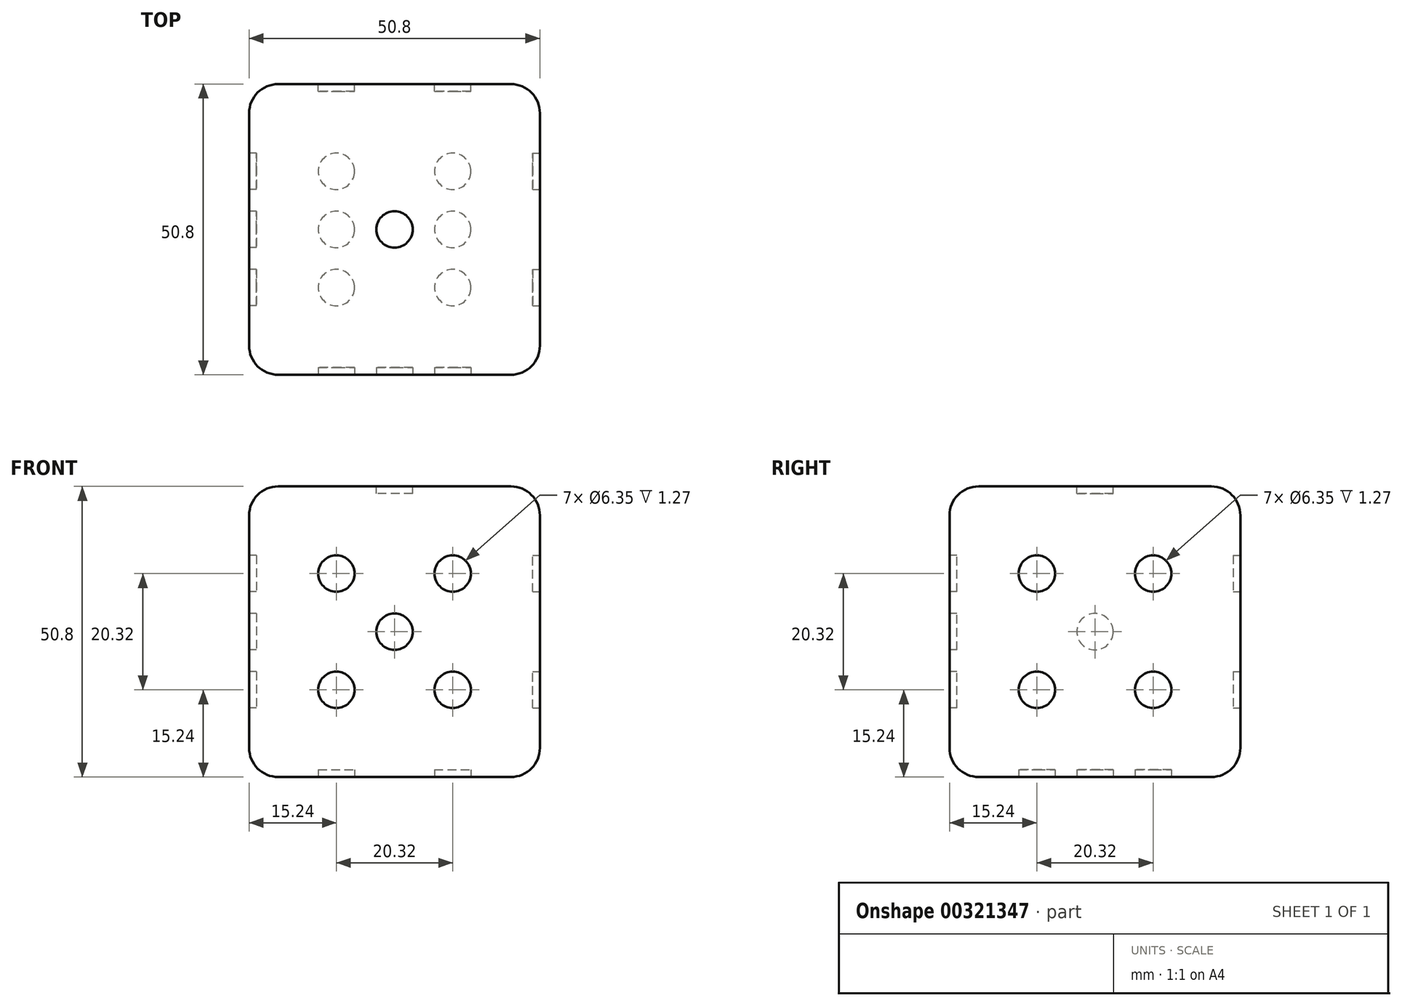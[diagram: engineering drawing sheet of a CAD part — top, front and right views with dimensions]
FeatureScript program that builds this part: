
annotation { "Feature Type Name" : "Feature", "Feature Type Description" : "" }
export const myFeature = defineFeature(function(context is Context, id is Id, definition is map)
    precondition{}
    {
        {
            var Q0;
            Q0=qCreatedBy(makeId("Top.planeOp"),FACE);
            var sketch = newSketch(context, id + "F0", { "sketchPlane" : qUnion([Q0])});
            skLineSegment(sketch, "E0.bottom", {"start": v(0, 0) * mm, "end": v(50.8, 0) * mm});
            skLineSegment(sketch, "E0.top", {"start": v(0, -50.8) * mm, "end": v(50.8, -50.8) * mm});
            skLineSegment(sketch, "E0.left", {"start": v(0, 0) * mm, "end": v(0, -50.8) * mm});
            skLineSegment(sketch, "E0.right", {"start": v(50.8, 0) * mm, "end": v(50.8, -50.8) * mm});
            skSolve(sketch);
        }
        {
            var Q0;
            Q0=makeQuery(id+"F0.imprint","IMPRINT",FACE,{"disambiguationData":[TD([[makeQuery(id+"F0.imprint","IMPRINT",EDGE,{"derivedFrom":sQuery(id+"F0.wireOp",EDGE,"E0.bottom")}),-1.0]])]});
            extrude(context, id + "F1", {"entities" : qUnion([Q0]), "depth" : 50.8 * mm});
        }
        {
            var Q0;
            Q0=makeQuery(id+"F1.opExtrude","SWEPT_EDGE",EDGE,{"disambiguationData":[OSD([sQuery(id+"F0.wireOp",EDGE,"E0.top"),sQuery(id+"F0.wireOp",EDGE,"E0.right")])]});
            var Q1;
            Q1=makeQuery(id+"F1.opExtrude","CAP_EDGE",EDGE,{"disambiguationData":[OSD([sQuery(id+"F0.wireOp",EDGE,"E0.right")])],"isStart":false});
            var Q2;
            Q2=makeQuery(id+"F1.opExtrude","CAP_EDGE",EDGE,{"disambiguationData":[OSD([sQuery(id+"F0.wireOp",EDGE,"E0.right")])],"isStart":true});
            var Q3;
            Q3=makeQuery(id+"F1.opExtrude","CAP_EDGE",EDGE,{"disambiguationData":[OSD([sQuery(id+"F0.wireOp",EDGE,"E0.top")])],"isStart":true});
            var Q4;
            Q4=makeQuery(id+"F1.opExtrude","CAP_EDGE",EDGE,{"disambiguationData":[OSD([sQuery(id+"F0.wireOp",EDGE,"E0.top")])],"isStart":false});
            var Q5;
            Q5=makeQuery(id+"F1.opExtrude","SWEPT_EDGE",EDGE,{"disambiguationData":[OSD([sQuery(id+"F0.wireOp",EDGE,"E0.top"),sQuery(id+"F0.wireOp",EDGE,"E0.left")])]});
            var Q6;
            Q6=makeQuery(id+"F1.opExtrude","SWEPT_EDGE",EDGE,{"disambiguationData":[OSD([sQuery(id+"F0.wireOp",EDGE,"E0.bottom"),sQuery(id+"F0.wireOp",EDGE,"E0.right")])]});
            var Q7;
            Q7=makeQuery(id+"F1.opExtrude","SWEPT_EDGE",EDGE,{"disambiguationData":[OSD([sQuery(id+"F0.wireOp",EDGE,"E0.bottom"),sQuery(id+"F0.wireOp",EDGE,"E0.left")])]});
            var Q8;
            Q8=makeQuery(id+"F1.opExtrude","CAP_EDGE",EDGE,{"disambiguationData":[OSD([sQuery(id+"F0.wireOp",EDGE,"E0.bottom")])],"isStart":false});
            var Q9;
            Q9=makeQuery(id+"F1.opExtrude","CAP_EDGE",EDGE,{"disambiguationData":[OSD([sQuery(id+"F0.wireOp",EDGE,"E0.bottom")])],"isStart":true});
            var Q10;
            Q10=makeQuery(id+"F1.opExtrude","CAP_EDGE",EDGE,{"disambiguationData":[OSD([sQuery(id+"F0.wireOp",EDGE,"E0.left")])],"isStart":false});
            var Q11;
            Q11=makeQuery(id+"F1.opExtrude","CAP_EDGE",EDGE,{"disambiguationData":[OSD([sQuery(id+"F0.wireOp",EDGE,"E0.left")])],"isStart":true});
            var Q12;
            Q12=makeQuery(id+"F1.opExtrude","CAP_FACE",FACE,{"disambiguationData":[OSD([sQuery(id+"F0.wireOp",EDGE,"E0.bottom"),sQuery(id+"F0.wireOp",EDGE,"E0.top"),sQuery(id+"F0.wireOp",EDGE,"E0.left"),sQuery(id+"F0.wireOp",EDGE,"E0.right")])],"isStart":false});
            fillet(context, id + "F2", {"entities" : qUnion([Q0, Q1, Q2, Q3, Q4, Q5, Q6, Q7, Q8, Q9, Q10, Q11, Q12]), "radius" : 5.08 * mm, "tangentPropagation" : true, "allowEdgeOverflow" : false});
        }
        {
            var Q0;
            Q0=makeQuery(id+"F1.opExtrude","CAP_FACE",FACE,{"disambiguationData":[OSD([sQuery(id+"F0.wireOp",EDGE,"E0.bottom"),sQuery(id+"F0.wireOp",EDGE,"E0.top"),sQuery(id+"F0.wireOp",EDGE,"E0.left"),sQuery(id+"F0.wireOp",EDGE,"E0.right")])],"isStart":false});
            var sketch = newSketch(context, id + "F3", { "sketchPlane" : qUnion([Q0])});
            skLineSegment(sketch, "E1", {"start": v(25.4, -5.08) * mm, "end": v(25.4, -45.72) * mm, "construction": true});
            skCircle(sketch, "E2", {"center": v(25.4, -25.4) * mm, "radius": 3.18 * mm});
            skSolve(sketch);
        }
        {
            var Q0;
            Q0=makeQuery(id+"F3.imprint","IMPRINT",FACE,{"disambiguationData":[TD([[makeQuery(id+"F3.imprint","IMPRINT",EDGE,{"derivedFrom":sQuery(id+"F3.wireOp",EDGE,"E2")}),1.0]])]});
            extrude(context, id + "F4", {"entities" : qUnion([Q0]), "operationType" : NewBodyOperationType.REMOVE, "oppositeDirection" : true, "depth" : 1.27 * mm});
        }
        {
            var Q0;
            Q0=makeQuery(id+"F1.opExtrude","CAP_FACE",FACE,{"disambiguationData":[OSD([sQuery(id+"F0.wireOp",EDGE,"E0.bottom"),sQuery(id+"F0.wireOp",EDGE,"E0.top"),sQuery(id+"F0.wireOp",EDGE,"E0.left"),sQuery(id+"F0.wireOp",EDGE,"E0.right")])],"isStart":true});
            var sketch = newSketch(context, id + "F5", { "sketchPlane" : qUnion([Q0])});
            skLineSegment(sketch, "E3", {"start": v(25.4, 45.72) * mm, "end": v(25.4, 5.08) * mm, "construction": true});
            skLineSegment(sketch, "E4", {"start": v(45.72, 25.4) * mm, "end": v(25.4, 25.4) * mm, "construction": true});
            skLineSegment(sketch, "E5", {"start": v(5.08, 25.4) * mm, "end": v(25.4, 25.4) * mm, "construction": true});
            skLineSegment(sketch, "E6", {"start": v(15.24, 25.4) * mm, "end": v(15.24, 5.08) * mm, "construction": true});
            skLineSegment(sketch, "E7", {"start": v(15.24, 25.4) * mm, "end": v(15.24, 45.72) * mm, "construction": true});
            skLineSegment(sketch, "E8", {"start": v(35.56, 25.4) * mm, "end": v(35.56, 45.72) * mm, "construction": true});
            skLineSegment(sketch, "E9", {"start": v(35.56, 25.4) * mm, "end": v(35.56, 5.08) * mm, "construction": true});
            skCircle(sketch, "E10", {"center": v(15.24, 15.24) * mm, "radius": 3.18 * mm});
            skCircle(sketch, "E11", {"center": v(35.56, 15.24) * mm, "radius": 3.18 * mm});
            skCircle(sketch, "E12", {"center": v(35.56, 35.56) * mm, "radius": 3.18 * mm});
            skCircle(sketch, "E13", {"center": v(15.24, 35.56) * mm, "radius": 3.18 * mm});
            skCircle(sketch, "E14", {"center": v(15.24, 25.4) * mm, "radius": 3.18 * mm});
            skCircle(sketch, "E15", {"center": v(35.56, 25.4) * mm, "radius": 3.18 * mm});
            skSolve(sketch);
        }
        {
            var Q0;
            Q0 = qSketchRegion(id + "F5", true);
            extrude(context, id + "F6", {"entities" : qUnion([Q0]), "operationType" : NewBodyOperationType.REMOVE, "oppositeDirection" : true, "depth" : 1.27 * mm});
        }
        {
            var Q0;
            Q0=makeQuery(id+"F1.opExtrude","SWEPT_FACE",FACE,{"disambiguationData":[OSD([sQuery(id+"F0.wireOp",EDGE,"E0.top")])]});
            var sketch = newSketch(context, id + "F7", { "sketchPlane" : qUnion([Q0])});
            skLineSegment(sketch, "E16", {"start": v(45.72, 25.4) * mm, "end": v(5.08, 25.4) * mm, "construction": true});
            skCircle(sketch, "E17", {"center": v(25.4, 25.4) * mm, "radius": 3.18 * mm});
            skLineSegment(sketch, "E18", {"start": v(25.4, 25.4) * mm, "end": v(25.4, 5.08) * mm, "construction": true});
            skLineSegment(sketch, "E19", {"start": v(25.4, 5.08) * mm, "end": v(25.4, 25.4) * mm, "construction": true});
            skLineSegment(sketch, "E20", {"start": v(25.4, 45.72) * mm, "end": v(25.4, 25.4) * mm, "construction": true});
            skLineSegment(sketch, "E21", {"start": v(25.4, 15.24) * mm, "end": v(45.72, 15.24) * mm, "construction": true});
            skLineSegment(sketch, "E22", {"start": v(25.4, 35.56) * mm, "end": v(45.72, 35.56) * mm});
            skLineSegment(sketch, "E23", {"start": v(25.4, 35.56) * mm, "end": v(5.08, 35.56) * mm, "construction": true});
            skLineSegment(sketch, "E24", {"start": v(25.4, 15.24) * mm, "end": v(5.08, 15.24) * mm, "construction": true});
            skCircle(sketch, "E25", {"center": v(35.56, 15.24) * mm, "radius": 3.18 * mm});
            skCircle(sketch, "E26", {"center": v(35.56, 35.56) * mm, "radius": 3.18 * mm});
            skCircle(sketch, "E27", {"center": v(15.24, 35.56) * mm, "radius": 3.18 * mm});
            skCircle(sketch, "E28", {"center": v(15.24, 15.24) * mm, "radius": 3.18 * mm});
            skSolve(sketch);
        }
        {
            var Q0;
            Q0 = qSketchRegion(id + "F7", true);
            extrude(context, id + "F8", {"entities" : qUnion([Q0]), "operationType" : NewBodyOperationType.REMOVE, "oppositeDirection" : true, "depth" : 1.27 * mm});
        }
        {
            var Q0;
            Q0=makeQuery(id+"F1.opExtrude","SWEPT_FACE",FACE,{"disambiguationData":[OSD([sQuery(id+"F0.wireOp",EDGE,"E0.bottom")])]});
            var sketch = newSketch(context, id + "F9", { "sketchPlane" : qUnion([Q0])});
            skLineSegment(sketch, "E29", {"start": v(-25.4, 45.72) * mm, "end": v(-25.4, 5.08) * mm, "construction": true});
            skLineSegment(sketch, "E30", {"start": v(-45.72, 25.4) * mm, "end": v(-5.08, 25.4) * mm, "construction": true});
            skLineSegment(sketch, "E31", {"start": v(-25.4, 25.4) * mm, "end": v(-5.08, 25.4) * mm, "construction": true});
            skLineSegment(sketch, "E32", {"start": v(-25.4, 25.4) * mm, "end": v(-45.72, 25.4) * mm, "construction": true});
            skLineSegment(sketch, "E33", {"start": v(-35.56, 25.4) * mm, "end": v(-35.56, 45.72) * mm, "construction": true});
            skLineSegment(sketch, "E34", {"start": v(-35.56, 45.72) * mm, "end": v(-35.56, 5.08) * mm, "construction": true});
            skLineSegment(sketch, "E35", {"start": v(-15.24, 25.4) * mm, "end": v(-15.24, 45.72) * mm, "construction": true});
            skLineSegment(sketch, "E36", {"start": v(-15.24, 45.72) * mm, "end": v(-15.24, 5.08) * mm, "construction": true});
            skLineSegment(sketch, "E37", {"start": v(-35.56, 25.4) * mm, "end": v(-35.56, 5.08) * mm, "construction": true});
            skCircle(sketch, "E38", {"center": v(-15.24, 35.56) * mm, "radius": 3.18 * mm});
            skCircle(sketch, "E39", {"center": v(-35.56, 15.24) * mm, "radius": 3.18 * mm});
            skSolve(sketch);
        }
        {
            var Q0;
            Q0 = qSketchRegion(id + "F9", true);
            extrude(context, id + "F10", {"entities" : qUnion([Q0]), "operationType" : NewBodyOperationType.REMOVE, "oppositeDirection" : true, "depth" : 1.27 * mm});
        }
        {
            var Q0;
            Q0=makeQuery(id+"F1.opExtrude","SWEPT_FACE",FACE,{"disambiguationData":[OSD([sQuery(id+"F0.wireOp",EDGE,"E0.left")])]});
            var sketch = newSketch(context, id + "F11", { "sketchPlane" : qUnion([Q0])});
            skLineSegment(sketch, "E40", {"start": v(25.4, 45.72) * mm, "end": v(25.4, 5.08) * mm, "construction": true});
            skLineSegment(sketch, "E41", {"start": v(25.4, 25.4) * mm, "end": v(45.72, 25.4) * mm, "construction": true});
            skLineSegment(sketch, "E42", {"start": v(25.4, 25.4) * mm, "end": v(5.08, 25.4) * mm, "construction": true});
            skLineSegment(sketch, "E43", {"start": v(35.56, 25.4) * mm, "end": v(35.56, 45.72) * mm, "construction": true});
            skLineSegment(sketch, "E44", {"start": v(35.56, 25.4) * mm, "end": v(35.56, 5.08) * mm, "construction": true});
            skLineSegment(sketch, "E45", {"start": v(15.24, 25.4) * mm, "end": v(15.24, 45.72) * mm, "construction": true});
            skLineSegment(sketch, "E46", {"start": v(15.24, 25.4) * mm, "end": v(15.24, 5.08) * mm, "construction": true});
            skCircle(sketch, "E47", {"center": v(25.4, 25.4) * mm, "radius": 3.17 * mm});
            skCircle(sketch, "E48", {"center": v(35.56, 35.56) * mm, "radius": 3.18 * mm});
            skCircle(sketch, "E49", {"center": v(15.24, 15.24) * mm, "radius": 3.18 * mm});
            skSolve(sketch);
        }
        {
            var Q0;
            Q0 = qSketchRegion(id + "F11", true);
            extrude(context, id + "F12", {"entities" : qUnion([Q0]), "operationType" : NewBodyOperationType.REMOVE, "oppositeDirection" : true, "depth" : 1.27 * mm});
        }
        {
            var Q0;
            Q0=makeQuery(id+"F1.opExtrude","SWEPT_FACE",FACE,{"disambiguationData":[OSD([sQuery(id+"F0.wireOp",EDGE,"E0.right")])]});
            var sketch = newSketch(context, id + "F13", { "sketchPlane" : qUnion([Q0])});
            skLineSegment(sketch, "E50", {"start": v(-25.4, 45.72) * mm, "end": v(-25.4, 5.08) * mm, "construction": true});
            skLineSegment(sketch, "E51", {"start": v(-25.4, 25.4) * mm, "end": v(-45.72, 25.4) * mm, "construction": true});
            skLineSegment(sketch, "E52", {"start": v(-25.4, 25.4) * mm, "end": v(-5.08, 25.4) * mm, "construction": true});
            skLineSegment(sketch, "E53", {"start": v(-15.24, 25.4) * mm, "end": v(-15.24, 45.72) * mm, "construction": true});
            skLineSegment(sketch, "E54", {"start": v(-15.24, 25.4) * mm, "end": v(-15.24, 5.08) * mm, "construction": true});
            skLineSegment(sketch, "E55", {"start": v(-35.56, 25.4) * mm, "end": v(-35.56, 45.72) * mm, "construction": true});
            skLineSegment(sketch, "E56", {"start": v(-35.56, 25.4) * mm, "end": v(-35.56, 5.08) * mm, "construction": true});
            skCircle(sketch, "E57", {"center": v(-15.24, 35.56) * mm, "radius": 3.18 * mm});
            skCircle(sketch, "E58", {"center": v(-35.56, 35.56) * mm, "radius": 3.18 * mm});
            skCircle(sketch, "E59", {"center": v(-35.56, 15.24) * mm, "radius": 3.18 * mm});
            skCircle(sketch, "E60", {"center": v(-15.24, 15.24) * mm, "radius": 3.18 * mm});
            skSolve(sketch);
        }
        {
            var Q0;
            Q0 = qSketchRegion(id + "F13", true);
            extrude(context, id + "F14", {"entities" : qUnion([Q0]), "operationType" : NewBodyOperationType.REMOVE, "oppositeDirection" : true, "depth" : 1.27 * mm});
        }
    });
